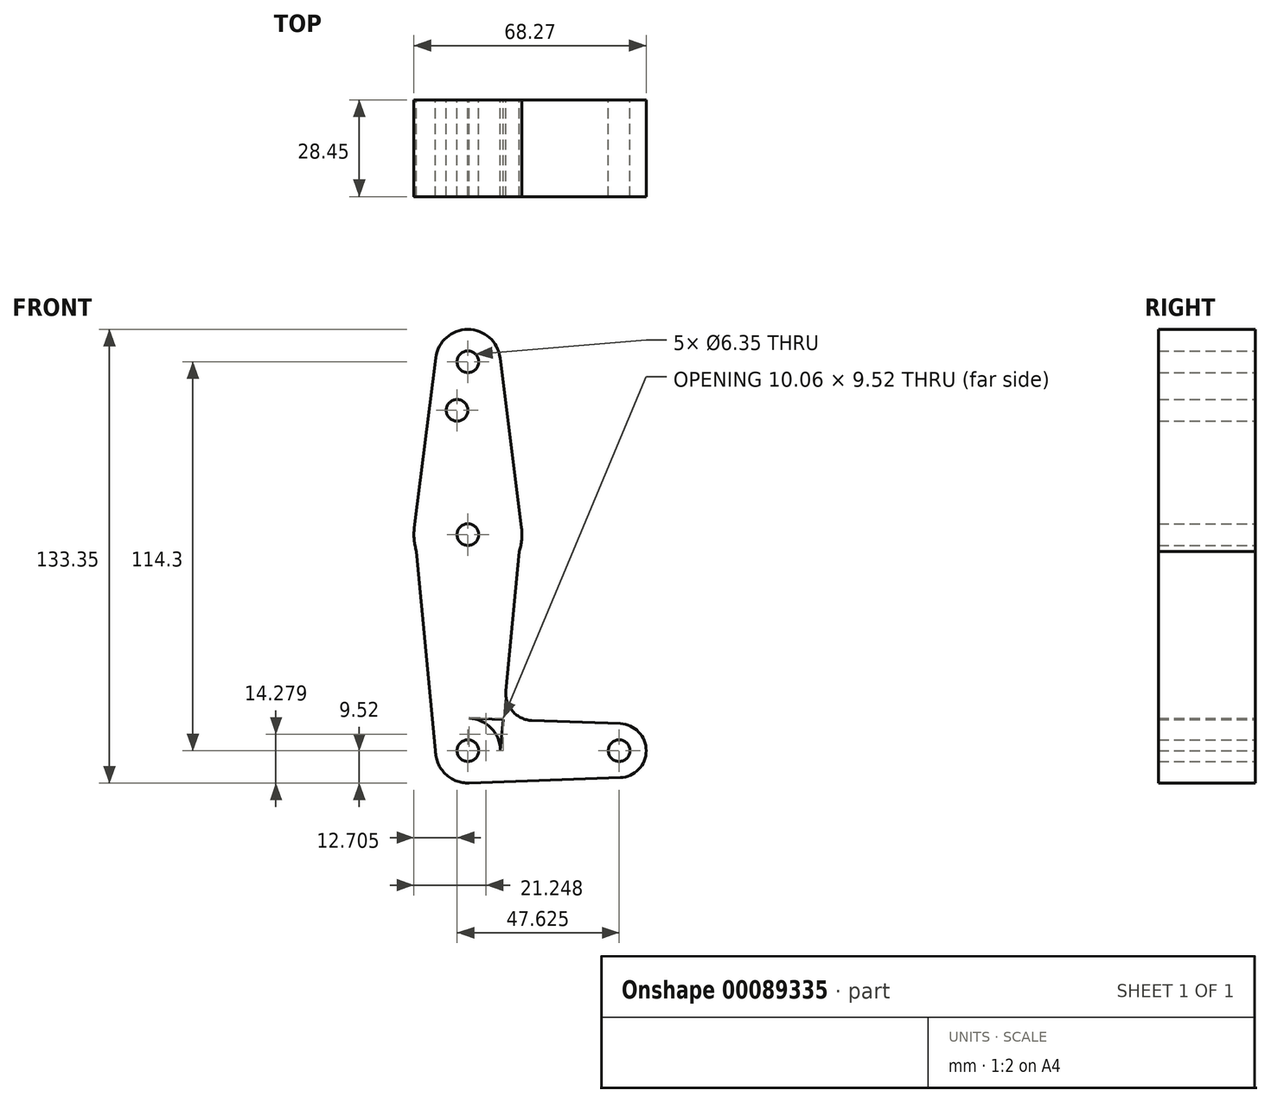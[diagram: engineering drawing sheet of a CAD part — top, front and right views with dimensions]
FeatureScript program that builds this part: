
annotation { "Feature Type Name" : "Feature", "Feature Type Description" : "" }
export const myFeature = defineFeature(function(context is Context, id is Id, definition is map)
    precondition{}
    {
        {
            var Q0;
            Q0=qCreatedBy(makeId("Front.planeOp"),FACE);
            var sketch = newSketch(context, id + "F0", { "sketchPlane" : qUnion([Q0])});
            skCircle(sketch, "E0", {"center": v(0, 114.3) * mm, "radius": 9.53 * mm});
            skCircle(sketch, "E1", {"center": v(0, 63.5) * mm, "radius": 15.88 * mm});
            skCircle(sketch, "E2", {"center": v(0, 0) * mm, "radius": 9.53 * mm});
            skCircle(sketch, "E3", {"center": v(44.45, 0) * mm, "radius": 7.94 * mm});
            skLineSegment(sketch, "E4", {"start": v(0, 114.3) * mm, "end": v(0, 63.5) * mm, "construction": true});
            skLineSegment(sketch, "E5", {"start": v(0, 0) * mm, "end": v(44.45, 0) * mm});
            skLineSegment(sketch, "E6", {"start": v(0, 63.5) * mm, "end": v(0, 0) * mm, "construction": true});
            skLineSegment(sketch, "E7", {"start": v(-9.45, 115.5) * mm, "end": v(-15.75, 65.48) * mm});
            skLineSegment(sketch, "E8", {"start": v(9.45, 115.5) * mm, "end": v(15.75, 65.48) * mm});
            skLineSegment(sketch, "E9", {"start": v(15.75, 65.48) * mm, "end": v(9.53, 0) * mm});
            skLineSegment(sketch, "E10", {"start": v(-15.75, 65.48) * mm, "end": v(-9.53, 0) * mm});
            skLineSegment(sketch, "E11", {"start": v(0.34, 9.52) * mm, "end": v(44.73, 7.93) * mm});
            skLineSegment(sketch, "E12", {"start": v(44.73, -7.93) * mm, "end": v(0.34, -9.52) * mm});
            skArc(sketch, "E13", {"start": v(11.2, 17.56) * mm, "mid": v(13.13, 11.56) * mm, "end": v(18.82, 8.86) * mm});
            skCircle(sketch, "E14", {"center": v(-3.18, 100.03) * mm, "radius": 3.18 * mm});
            skCircle(sketch, "E15", {"center": v(0, 114.3) * mm, "radius": 3.18 * mm});
            skCircle(sketch, "E16", {"center": v(0, 63.5) * mm, "radius": 3.18 * mm});
            skCircle(sketch, "E17", {"center": v(0, 0) * mm, "radius": 3.18 * mm});
            skCircle(sketch, "E18", {"center": v(44.45, 0) * mm, "radius": 3.18 * mm});
            skSolve(sketch);
        }
        {
            var Q0;
            Q0 = qSketchRegion(id + "F0", true);
            extrude(context, id + "F1", {"entities" : qUnion([Q0]), "depth" : 28.45 * mm});
        }
    });
